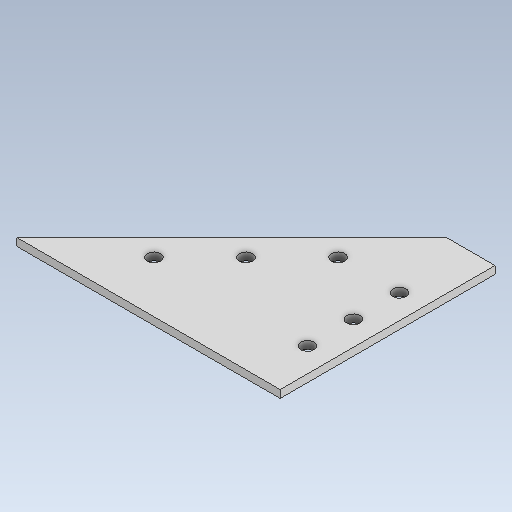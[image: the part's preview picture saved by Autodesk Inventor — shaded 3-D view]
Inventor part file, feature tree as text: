
AUTODESK INVENTOR PART (.ipt)
format: ipt  version: 2023 (Build 270158000, 158)  size: 113,664 bytes
history: native  units: in
note: dims shown in document units (in); Inventor stores cm internally (conversion verified against a paired STEP export)
features: sketch x1, extrude x1, hole x1
ambient origin geometry x8: Origin, YZ Plane, XZ Plane, XY Plane, X Axis, Y Axis, Z Axis, Center Point
bodies: Solid1 (feature_tree)
feature tree (3):
  sketch  "Sketch1"  dims[d0=4.0in d1=4.0in d2=0.7874in d3=0.7874in d4=45.0deg d11=0.3937in d13=0.3937in d15=1.0in d16=1.5in d17=3.5in d19=0.125in d20=0.0in d21=0.217in d22=0.472in d23=0.409in d24=0.25in d25=90.0deg d26=1.0in d27=0.8108in d28=0.0in d29=0.0in d30=0.0in d31=0.0in]
  extrude  "Extrusion1"  Depth=0.125in
  hole  "Hole1"  [1 undecoded]
note: 1 required parameter value undecoded (feature->parameter linkage not recoverable at this tier; creation-order binding heuristic only, values carry confidence <= 0.55)
